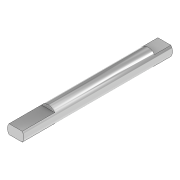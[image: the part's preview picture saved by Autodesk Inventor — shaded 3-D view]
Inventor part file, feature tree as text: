
AUTODESK INVENTOR PART (.ipt)
format: ipt  version: 2020 (Build 240168000, 168)  size: 100,864 bytes
history: native  units: in
note: dims shown in document units (in); Inventor stores cm internally (conversion verified against a paired STEP export)
features: extrude x3, sketch x3, projected_geometry x2
ambient origin geometry x8: Origin, YZ Plane, XZ Plane, XY Plane, X Axis, Y Axis, Z Axis, Center Point
bodies: Solid1 (feature_tree)
feature tree (8):
  extrude  "Extrusion1"  Depth=1.8012in TaperAngle=0.0deg
  extrude  "Extrusion2"  Depth=0.1181in
  extrude  "Extrusion3"  Depth=0.1142in
  sketch  "Sketch1"  dims[d0=0.1969in d1=1.8012in d2=0.0in]
  sketch  "Sketch2"  dims[d3=0.0591in d4=0.1181in]
  projected_geometry  "Projected Loop1"
  sketch  "Sketch3"  dims[d5=0.1969in d6=0.0in d7=0.1142in d8=0.0571in d9=0.3937in d10=0.0in]
  projected_geometry  "Projected Loop2"
